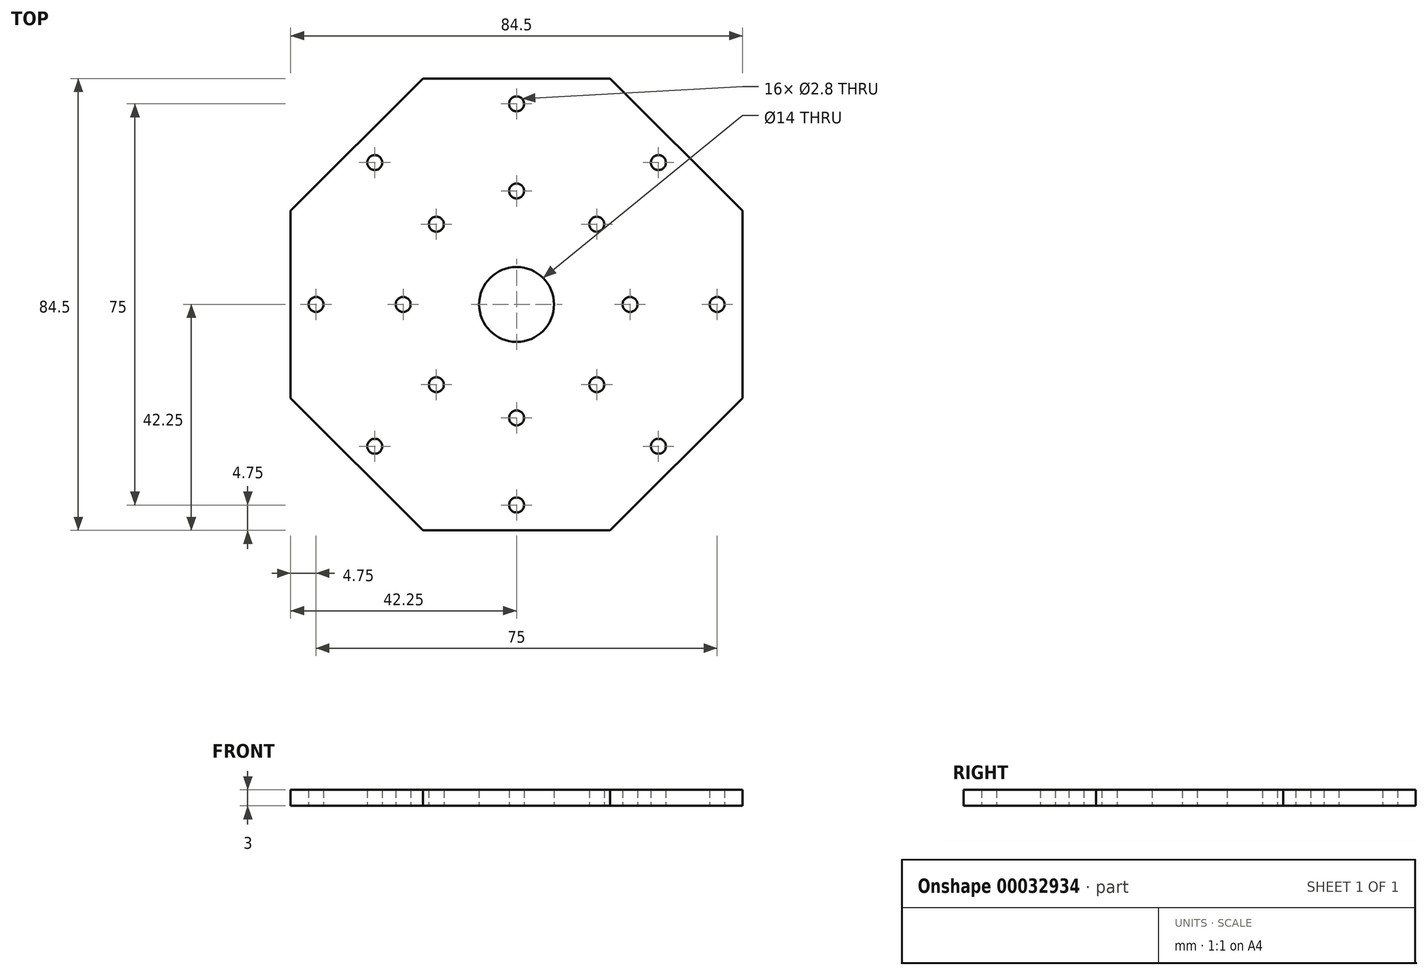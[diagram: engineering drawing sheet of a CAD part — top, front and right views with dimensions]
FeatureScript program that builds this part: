
annotation { "Feature Type Name" : "Feature", "Feature Type Description" : "" }
export const myFeature = defineFeature(function(context is Context, id is Id, definition is map)
    precondition{}
    {
        {
            var Q0;
            Q0=qCreatedBy(makeId("Top.planeOp"),FACE);
            var sketch = newSketch(context, id + "F0", { "sketchPlane" : qUnion([Q0])});
            skLineSegment(sketch, "E0.rect.bottom", {"start": v(15, -15) * mm, "end": v(-15, -15) * mm, "construction": true});
            skLineSegment(sketch, "E0.rect.top", {"start": v(15, 15) * mm, "end": v(-15, 15) * mm, "construction": true});
            skLineSegment(sketch, "E0.rect.left", {"start": v(15, -15) * mm, "end": v(15, 15) * mm, "construction": true});
            skLineSegment(sketch, "E0.rect.right", {"start": v(-15, -15) * mm, "end": v(-15, 15) * mm, "construction": true});
            skPoint(sketch, "E0.rect.middle", {"position": v(0, 0) * mm});
            skCircle(sketch, "E1.cCircle", {"center": v(0, 0) * mm, "radius": 21.21 * mm, "construction": true});
            skLineSegment(sketch, "E1.0", {"start": v(21.21, 0) * mm, "end": v(0, -21.21) * mm, "construction": true});
            skLineSegment(sketch, "E1.1", {"start": v(0, -21.21) * mm, "end": v(-21.21, 0) * mm, "construction": true});
            skLineSegment(sketch, "E1.2", {"start": v(-21.21, 0) * mm, "end": v(0, 21.21) * mm, "construction": true});
            skLineSegment(sketch, "E1.3", {"start": v(0, 21.21) * mm, "end": v(21.21, 0) * mm, "construction": true});
            skCircle(sketch, "E2", {"center": v(0, 21.21) * mm, "radius": 1.4 * mm});
            skCircle(sketch, "E3.1.0", {"center": v(-15, 15) * mm, "radius": 1.4 * mm});
            skCircle(sketch, "E3.2.0", {"center": v(-21.21, 0) * mm, "radius": 1.4 * mm});
            skCircle(sketch, "E3.3.0", {"center": v(-15, -15) * mm, "radius": 1.4 * mm});
            skCircle(sketch, "E3.4.0", {"center": v(0, -21.21) * mm, "radius": 1.4 * mm});
            skCircle(sketch, "E3.5.0", {"center": v(15, -15) * mm, "radius": 1.4 * mm});
            skCircle(sketch, "E3.6.0", {"center": v(21.21, 0) * mm, "radius": 1.4 * mm});
            skCircle(sketch, "E3.7.0", {"center": v(15, 15) * mm, "radius": 1.4 * mm});
            skCircle(sketch, "E4.cCircle", {"center": v(0, 0) * mm, "radius": 42.25 * mm, "construction": true});
            skLineSegment(sketch, "E4.0", {"start": v(-17.5, 42.25) * mm, "end": v(17.5, 42.25) * mm});
            skLineSegment(sketch, "E4.1", {"start": v(17.5, 42.25) * mm, "end": v(42.25, 17.5) * mm});
            skLineSegment(sketch, "E4.2", {"start": v(42.25, 17.5) * mm, "end": v(42.25, -17.5) * mm});
            skLineSegment(sketch, "E4.3", {"start": v(42.25, -17.5) * mm, "end": v(17.5, -42.25) * mm});
            skLineSegment(sketch, "E4.4", {"start": v(17.5, -42.25) * mm, "end": v(-17.5, -42.25) * mm});
            skLineSegment(sketch, "E4.5", {"start": v(-17.5, -42.25) * mm, "end": v(-42.25, -17.5) * mm});
            skLineSegment(sketch, "E4.6", {"start": v(-42.25, -17.5) * mm, "end": v(-42.25, 17.5) * mm});
            skLineSegment(sketch, "E4.7", {"start": v(-42.25, 17.5) * mm, "end": v(-17.5, 42.25) * mm});
            skPoint(sketch, "E4.0.midPoint", {"position": v(0, 42.25) * mm});
            skCircle(sketch, "E5", {"center": v(0, 0) * mm, "radius": 7 * mm});
            skCircle(sketch, "E6", {"center": v(0, 0) * mm, "radius": 37.5 * mm, "construction": true});
            skLineSegment(sketch, "E7", {"start": v(0, 0) * mm, "end": v(26.52, 26.52) * mm, "construction": true});
            skCircle(sketch, "E8", {"center": v(26.52, 26.52) * mm, "radius": 1.4 * mm});
            skCircle(sketch, "E9.1.0", {"center": v(0, 37.5) * mm, "radius": 1.4 * mm});
            skCircle(sketch, "E9.2.0", {"center": v(-26.52, 26.52) * mm, "radius": 1.4 * mm});
            skCircle(sketch, "E9.3.0", {"center": v(-37.5, 0) * mm, "radius": 1.4 * mm});
            skCircle(sketch, "E10.1.4.0", {"center": v(-26.52, -26.52) * mm, "radius": 1.4 * mm});
            skCircle(sketch, "E10.1.5.0", {"center": v(0, -37.5) * mm, "radius": 1.4 * mm});
            skCircle(sketch, "E10.1.6.0", {"center": v(26.52, -26.52) * mm, "radius": 1.4 * mm});
            skCircle(sketch, "E10.1.7.0", {"center": v(37.5, 0) * mm, "radius": 1.4 * mm});
            skSolve(sketch);
        }
        {
            var Q0;
            Q0=makeQuery(id+"F0.imprint","IMPRINT",FACE,{"disambiguationData":[TD([[makeQuery(id+"F0.imprint","IMPRINT",EDGE,{"derivedFrom":sQuery(id+"F0.wireOp",EDGE,"E2")}),-1.0]])]});
            extrude(context, id + "F1", {"entities" : qUnion([Q0]), "depth" : 3 * mm});
        }
    });
